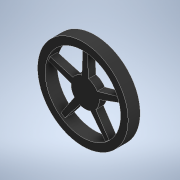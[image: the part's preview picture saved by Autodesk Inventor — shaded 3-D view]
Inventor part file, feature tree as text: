
AUTODESK INVENTOR PART (.ipt)
format: ipt  version: 2022 (Build 260153000, 153)  size: 153,088 bytes
history: native  units: mm
features: extrude x4, sketch x4, other x1, pattern_circular x1
ambient origin geometry x8: Origin, YZ Plane, XZ Plane, XY Plane, X Axis, Y Axis, Z Axis, Center Point
bodies: Body1 (feature_tree)
feature tree (10):
  other  "ソリッド1"
  extrude  "押し出し1"  Depth=60.0mm
  extrude  "押し出し2"  Depth=5.0mm
  pattern_circular  "円形状パターン1"  [2 undecoded]
  extrude  "押し出し3"  Depth=18.7mm
  extrude  "押し出し4"  Depth=5.0mm
  sketch  "スケッチ1"
  sketch  "スケッチ2"
  sketch  "スケッチ3"
  sketch  "スケッチ4"
note: 2 required parameter values undecoded (feature->parameter linkage not recoverable at this tier; creation-order binding heuristic only, values carry confidence <= 0.55)
